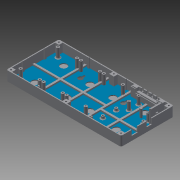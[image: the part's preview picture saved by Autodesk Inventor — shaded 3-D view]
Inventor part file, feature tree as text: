
AUTODESK INVENTOR PART (.ipt)
format: ipt  version: 2015 (Build 190159000, 159)  size: 645,120 bytes
history: native  units: mm
features: extrude x23, sketch x23, pattern_linear x2, fillet x2, other x1
ambient origin geometry x8: Origin, YZ Plane, XZ Plane, XY Plane, X Axis, Y Axis, Z Axis, Center Point
bodies: Body1 (feature_tree)
feature tree (51):
  other  "ソリッド1"
  extrude  "底"  Depth=240.0mm
  extrude  "底 くりぬき"  Depth=110.0mm
  extrude  "天板固定用ボス"  Depth=120.0mm
  extrude  "天板固定用穴"  Depth=55.0mm
  extrude  "天板固定用穴ザグリ"  Depth=20.0mm TaperAngle=0.0deg
  extrude  "7セグ固定用ボス"  Depth=236.0mm
  extrude  "7セグ固定用ボス ねじ穴"  Depth=106.0mm
  pattern_linear  "矩形状パターン1"  Spacing1=118.0mm  [1 undecoded]
  extrude  "Arduinoコネクタ穴"  Depth=53.0mm
  extrude  "Arduino固定用ボス"  Depth=18.0mm TaperAngle=0.0deg
  extrude  "Arduino固定用ボス ねじ穴"  Depth=8.0mm
  extrude  "タクトスイッチ穴"  Depth=8.0mm
  pattern_linear  "矩形状パターン2"  Spacing1=8.0mm  [1 undecoded]
  extrude  "タクトスイッチ固定用ボス"  Depth=8.0mm
  extrude  "タクトスイッチ基板用スリット"  Depth=8.0mm
  extrude  "タクトスイッチ基板用くりぬき1"  Depth=8.0mm
  extrude  "タクトスイッチ基板用くりぬき2"  Depth=8.0mm
  extrude  "LCD RTC基板固定用ボス"  Depth=18.0mm TaperAngle=0.0deg
  extrude  "LCD RTC基板固定用ボス ねじ穴"  Depth=3.2mm
  extrude  "LCD支持用ボス"  Depth=5.0mm
  extrude  "LCD支持用ボス くぼみ"  Depth=5.0mm
  fillet  "フィレット1"  Radius=3.2mm
  extrude  "壁掛けねじ穴"  Depth=5.0mm
  extrude  "磁石用くぼみ"  Depth=5.0mm
  extrude  "位置合わせ爪"  Depth=3.2mm
  fillet  "フィレット2"  Radius=5.0mm
  extrude  "底面 補強材"  Depth=5.0mm
  sketch  "スケッチ1"
  sketch  "スケッチ2"
  sketch  "スケッチ3"
  sketch  "スケッチ4"
  sketch  "スケッチ5"
  sketch  "スケッチ6"
  sketch  "スケッチ7"
  sketch  "スケッチ8"
  sketch  "スケッチ9"
  sketch  "スケッチ10"
  sketch  "スケッチ11"
  sketch  "スケッチ12"
  sketch  "スケッチ13"
  sketch  "スケッチ14"
  sketch  "スケッチ15"
  sketch  "スケッチ16"
  sketch  "スケッチ17"
  sketch  "スケッチ18"
  sketch  "スケッチ19"
  sketch  "スケッチ20"
  sketch  "スケッチ21"
  sketch  "スケッチ22"
  sketch  "スケッチ23"
note: 2 required parameter values undecoded (feature->parameter linkage not recoverable at this tier; creation-order binding heuristic only, values carry confidence <= 0.55)
